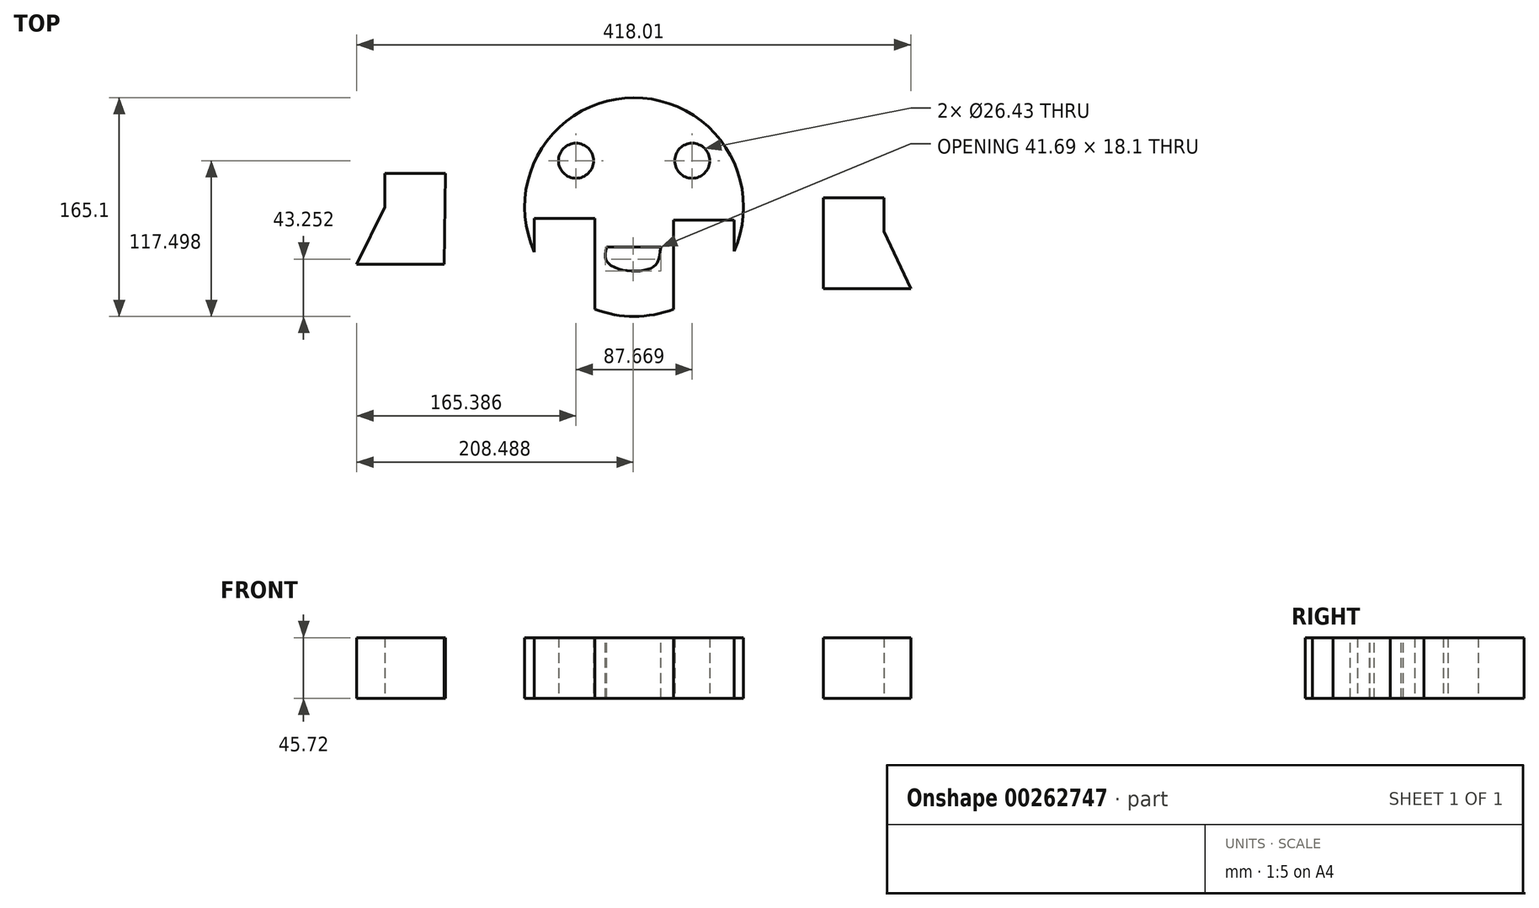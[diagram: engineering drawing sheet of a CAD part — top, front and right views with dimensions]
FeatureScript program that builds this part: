
annotation { "Feature Type Name" : "Feature", "Feature Type Description" : "" }
export const myFeature = defineFeature(function(context is Context, id is Id, definition is map)
    precondition{}
    {
        {
            var Q0;
            Q0=qCreatedBy(makeId("Top.planeOp"),FACE);
            var sketch = newSketch(context, id + "F0", { "sketchPlane" : qUnion([Q0])});
            skCircle(sketch, "E0", {"center": v(0, 0) * mm, "radius": 82.55 * mm});
            skCircle(sketch, "E1", {"center": v(-43.83, 34.95) * mm, "radius": 13.22 * mm});
            skLineSegment(sketch, "E2", {"start": v(2.23, -34.44) * mm, "end": v(-25.7, -34.74) * mm});
            skFitSpline(sketch, "E3", {"points": [v(-25.7, -34.74) * mm, v(-25.7, -48.46) * mm, v(-1.07, -63.95) * mm], "startDerivative": vector(7.07, -50.34) * mm, "endDerivative": vector(97.92, -5.11) * mm});
            skCircle(sketch, "E4.MirrorC", {"center": v(43.83, 34.95) * mm, "radius": 13.22 * mm});
            skLineSegment(sketch, "E5.MirrorCS", {"start": v(0, -34.4) * mm, "end": v(35.01, -35.01) * mm});
            skFitSpline(sketch, "E6.MirrorCS", {"points": [v(35.01, -35.01) * mm, v(33.52, -51.4) * mm, v(0, -63.73) * mm], "startDerivative": vector(5.94, -60.8) * mm, "endDerivative": vector(-96.9, -12.78) * mm});
            skSolve(sketch);
        }
        {
            var Q0;
            Q0 = qSketchRegion(id + "F0", true);
            extrude(context, id + "F1", {"entities" : qUnion([Q0]), "depth" : 45.72 * mm});
        }
        {
            var Q0;
            Q0=makeQuery(id+"F1.opExtrude","CAP_FACE",FACE,{"disambiguationData":[OSD([sQuery(id+"F0.wireOp",EDGE,"E0"),sQuery(id+"F0.wireOp",EDGE,"E1"),sQuery(id+"F0.wireOp",EDGE,"E4.MirrorC")])],"isStart":false});
            var sketch = newSketch(context, id + "F2", { "sketchPlane" : qUnion([Q0])});
            skLineSegment(sketch, "E7", {"start": v(-20.71, -30.25) * mm, "end": v(20.11, -30.25) * mm});
            skFitSpline(sketch, "E8", {"points": [v(-20.71, -30.25) * mm, v(-20.71, -40.68) * mm, v(-8.5, -47.53) * mm, v(8.2, -47.53) * mm, v(16.84, -43.06) * mm, v(20.11, -30.25) * mm], "startDerivative": vector(-13.23, -61.95) * mm, "endDerivative": vector(8.13, 72.13) * mm});
            skSolve(sketch);
        }
        {
            var Q0;
            Q0 = qSketchRegion(id + "F2", true);
            extrude(context, id + "F3", {"entities" : qUnion([Q0]), "operationType" : NewBodyOperationType.REMOVE, "oppositeDirection" : true, "depth" : 45.72 * mm});
        }
        {
            var Q0;
            Q0=makeQuery(id+"F1.opExtrude","CAP_FACE",FACE,{"disambiguationData":[OSD([sQuery(id+"F0.wireOp",EDGE,"E0"),sQuery(id+"F0.wireOp",EDGE,"E1"),sQuery(id+"F0.wireOp",EDGE,"E4.MirrorC")])],"isStart":false});
            var sketch = newSketch(context, id + "F4", { "sketchPlane" : qUnion([Q0])});
            skLineSegment(sketch, "E9", {"start": v(-75.27, -33.9) * mm, "end": v(-75.27, -8.5) * mm});
            skLineSegment(sketch, "E10", {"start": v(-75.27, -8.5) * mm, "end": v(-29.55, -8.5) * mm});
            skLineSegment(sketch, "E11", {"start": v(-29.55, -8.5) * mm, "end": v(-29.55, -77.08) * mm});
            skLineSegment(sketch, "E12.MirrorCS", {"start": v(75.5, -9.98) * mm, "end": v(29.77, -9.98) * mm});
            skLineSegment(sketch, "E13.MirrorCS", {"start": v(29.77, -8.42) * mm, "end": v(29.77, -77) * mm});
            skLineSegment(sketch, "E14.MirrorCS", {"start": v(75.5, -33.4) * mm, "end": v(75.5, -8) * mm});
            skSolve(sketch);
        }
        {
            var Q0;
            Q0 = qSketchRegion(id + "F4", true);
            var Q1;
            {var subQ0=sQuery(id+"F4.wireOp",EDGE,"E9");Q1=makeQuery(id+"F4.imprint","IMPRINT",FACE,{"disambiguationData":[TD([[makeQuery(id+"F4.imprint","IMPRINT",EDGE,{"derivedFrom":subQ0}),-1.0]])]});}
            var Q2;
            Q2=makeQuery(id+"F4.imprint","IMPRINT",FACE,{"disambiguationData":[TD([[makeQuery(id+"F4.imprint","IMPRINT",EDGE,{"derivedFrom":sQuery(id+"F4.wireOp",EDGE,"E12.MirrorCS")}),1.0]])]});
            extrude(context, id + "F5", {"entities" : qUnion([Q0, Q1, Q2]), "operationType" : NewBodyOperationType.REMOVE, "oppositeDirection" : true, "depth" : 45.72 * mm});
        }
        {
            var Q0;
            Q0=qCreatedBy(makeId("Top.planeOp"),FACE);
            var sketch = newSketch(context, id + "F6", { "sketchPlane" : qUnion([Q0])});
            skLineSegment(sketch, "E15", {"start": v(-187.95, 25.4) * mm, "end": v(-142.23, 25.4) * mm});
            skLineSegment(sketch, "E16", {"start": v(-142.23, 25.4) * mm, "end": v(-143.18, -43.17) * mm});
            skLineSegment(sketch, "E17", {"start": v(-143.18, -43.17) * mm, "end": v(-209.22, -43.17) * mm});
            skLineSegment(sketch, "E18", {"start": v(-187.95, 25.4) * mm, "end": v(-187.95, 0) * mm});
            skLineSegment(sketch, "E19", {"start": v(-187.95, 0) * mm, "end": v(-209.22, -43.17) * mm});
            skSolve(sketch);
        }
        {
            var Q0;
            Q0 = qSketchRegion(id + "F6", true);
            extrude(context, id + "F7", {"entities" : qUnion([Q0]), "depth" : 45.72 * mm});
        }
        {
            var Q0;
            Q0=qCreatedBy(makeId("Top.planeOp"),FACE);
            var sketch = newSketch(context, id + "F8", { "sketchPlane" : qUnion([Q0])});
            skLineSegment(sketch, "E20", {"start": v(142.75, 7.02) * mm, "end": v(188.47, 7.02) * mm});
            skLineSegment(sketch, "E21", {"start": v(188.47, 7.02) * mm, "end": v(188.47, -18.38) * mm});
            skLineSegment(sketch, "E22", {"start": v(142.75, 7.02) * mm, "end": v(142.75, -61.56) * mm});
            skLineSegment(sketch, "E23", {"start": v(188.47, -18.38) * mm, "end": v(208.79, -61.56) * mm});
            skLineSegment(sketch, "E24", {"start": v(208.79, -61.56) * mm, "end": v(142.75, -61.56) * mm});
            skSolve(sketch);
        }
        {
            var Q0;
            Q0 = qSketchRegion(id + "F8", true);
            extrude(context, id + "F9", {"entities" : qUnion([Q0]), "depth" : 45.72 * mm});
        }
    });
